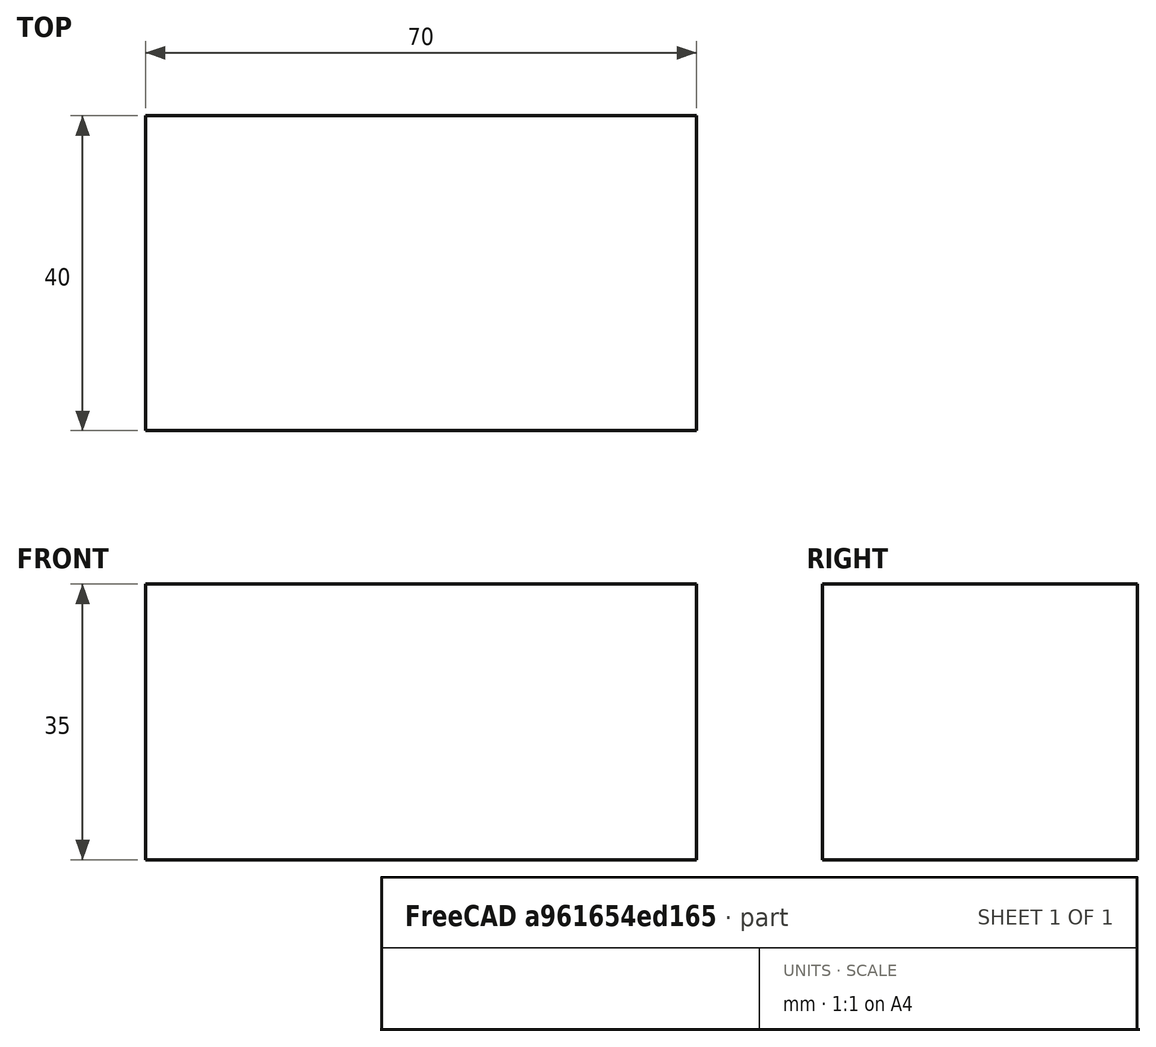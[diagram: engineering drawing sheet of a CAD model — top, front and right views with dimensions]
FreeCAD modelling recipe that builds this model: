
FCSTD DOCUMENT  (FreeCAD 0.19R24291 (Git))
Label: Attachment
License: All rights reserved
LicenseURL: http://en.wikipedia.org/wiki/All_rights_reserved
objects: Sketcher::SketchObject×2, PartDesign::Pad×1, PartDesign::Body×1
note: 5 computed .brp shape members not serialized (recipe doc carries the construction recipe); baked Part::Feature solids carry a one-line shape summary decoded from their .brp

FEATURE [Sketcher::SketchObject] Sketch  label="BaseSketch"
  FullyConstrained = true
  MapMode = 5
  Support = -> [XY_Plane]
  sketch-geometry (4):
    g0: LineSegment StartX=-35 StartY=20 StartZ=0 EndX=35 EndY=20 EndZ=0
    g1: LineSegment StartX=35 StartY=20 StartZ=0 EndX=35 EndY=-20 EndZ=0
    g2: LineSegment StartX=35 StartY=-20 StartZ=0 EndX=-35 EndY=-20 EndZ=0
    g3: LineSegment StartX=-35 StartY=-20 StartZ=0 EndX=-35 EndY=20 EndZ=0
  constraints (11):
    c: Coincident(g0,g1)
    c: Coincident(g1,g2)
    c: Coincident(g2,g3)
    c: Coincident(g3,g0)
    c: Horizontal(g0)
    c: Horizontal(g2)
    c: Vertical(g1)
    c: Vertical(g3)
    c: DistanceX(g0,g0) = 70  'length'
    c: DistanceY(g1,g0) = 40  'width'
    c: Symmetric(g0,g1,g-1)
FEATURE [PartDesign::Pad] Pad
  Direction = (1,1,1)
  Length = 35
  Length2 = 100
  Midplane = true
  Profile = -> Sketch
  Type = 0
  expr: Length = <<BaseSketch>>.Constraints.length / 2
FEATURE [Sketcher::SketchObject] Sketch001  label="IsoscelesSketch"
  FullyConstrained = false
  MapMode = 7
  Placement = pos=(35,-20,0) rot=(0.57735,0.57735,0.57735;2.0944rad)
  Support = -> [Sketch]
  expr: Constraints[6] = Sketch.Constraints.width / 2
  sketch-geometry (3):
    g0: LineSegment StartX=10.6691 StartY=96.2248 StartZ=0 EndX=10.6691 EndY=76.2248 EndZ=0
    g1: LineSegment StartX=10.6691 StartY=76.2248 StartZ=0 EndX=30.6691 EndY=96.2248 EndZ=0
    g2: LineSegment StartX=30.6691 StartY=96.2248 StartZ=0 EndX=10.6691 EndY=96.2248 EndZ=0
  constraints (7):
    c: Vertical(g0)
    c: Coincident(g0,g1)
    c: Coincident(g1,g2)
    c: Coincident(g2,g0)
    c: Equal(g2,g0)
    c: Perpendicular(g0,g2)
    c: DistanceX(g2,g2) = 20
FEATURE [PartDesign::Body] Body
  Group = -> [Sketch,Pad,Sketch001]
  Origin = -> Origin
  Tip = -> Pad
